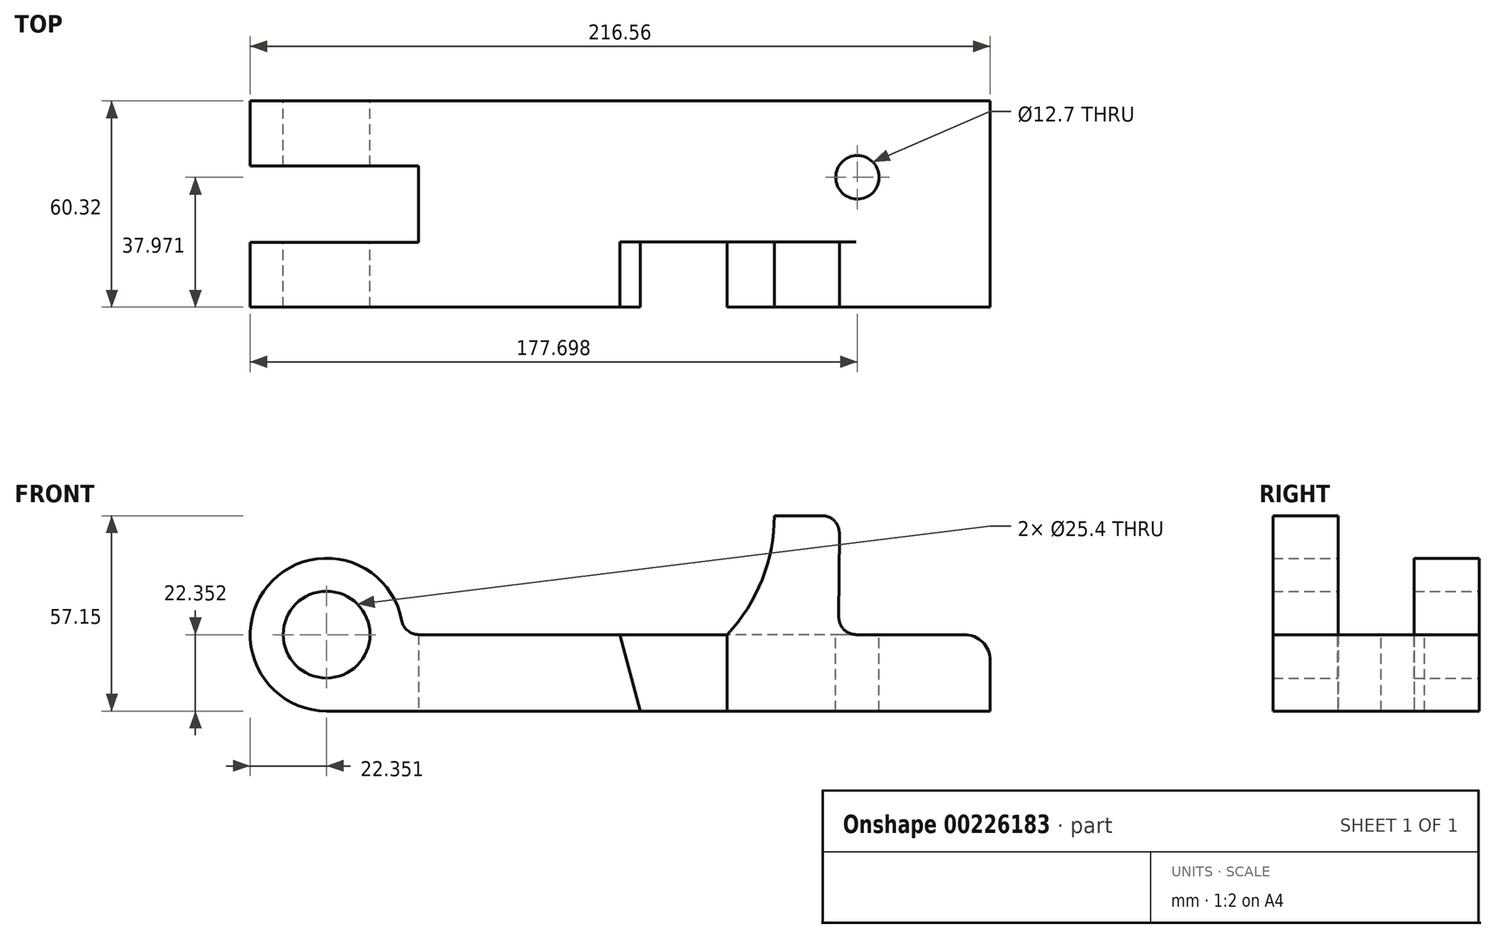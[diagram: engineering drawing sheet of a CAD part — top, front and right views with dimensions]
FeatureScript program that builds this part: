
annotation { "Feature Type Name" : "Feature", "Feature Type Description" : "" }
export const myFeature = defineFeature(function(context is Context, id is Id, definition is map)
    precondition{}
    {
        {
            var Q0;
            Q0=qCreatedBy(makeId("Front.planeOp"),FACE);
            var sketch = newSketch(context, id + "F0", { "sketchPlane" : qUnion([Q0])});
            skLineSegment(sketch, "E0.top", {"start": v(113.97, 22.35) * mm, "end": v(-57.89, 22.35) * mm});
            skLineSegment(sketch, "E0.left", {"start": v(113.97, 0) * mm, "end": v(113.97, 22.35) * mm});
            skCircle(sketch, "E1", {"center": v(-80.24, 22.35) * mm, "radius": 22.35 * mm});
            skCircle(sketch, "E2", {"center": v(-80.24, 22.35) * mm, "radius": 12.7 * mm});
            skLineSegment(sketch, "E3", {"start": v(-80.24, 0) * mm, "end": v(113.97, 0) * mm});
            skPoint(sketch, "E4", {"position": v(11.6, 0) * mm});
            skPoint(sketch, "E5", {"position": v(5.61, 22.35) * mm});
            skLineSegment(sketch, "E6", {"start": v(5.61, 22.35) * mm, "end": v(11.6, 0) * mm});
            skPoint(sketch, "E7", {"position": v(37, 0) * mm});
            skLineSegment(sketch, "E8", {"start": v(37, 0) * mm, "end": v(37, 22.35) * mm});
            skLineSegment(sketch, "E9.top", {"start": v(50.8, 57.15) * mm, "end": v(69.85, 57.15) * mm});
            skLineSegment(sketch, "E9.right", {"start": v(69.5, 0) * mm, "end": v(69.85, 57.15) * mm});
            skArc(sketch, "E10", {"start": v(37, 22.35) * mm, "mid": v(47.23, 38.43) * mm, "end": v(50.8, 57.15) * mm});
            skSolve(sketch);
        }
        {
            var Q0;
            {var subQ3=sQuery(id+"F0.wireOp",EDGE,"E6");Q0=makeQuery(id+"F0.imprint","IMPRINT",FACE,{"disambiguationData":[TD([[makeQuery(id+"F0.imprint","IMPRINT",EDGE,{"derivedFrom":subQ3}),-1.0]])]});}
            var Q1;
            {var subQ0=sQuery(id+"F0.wireOp",EDGE,"E8");Q1=makeQuery(id+"F0.imprint","IMPRINT",FACE,{"disambiguationData":[TD([[makeQuery(id+"F0.imprint","IMPRINT",EDGE,{"derivedFrom":subQ0}),-1.0]])]});}
            var Q2;
            {var subQ5=sQuery(id+"F0.wireOp",EDGE,"E9.bottom");Q2=makeQuery(id+"F0.imprint","IMPRINT",FACE,{"disambiguationData":[TD([[makeQuery(id+"F0.imprint","IMPRINT",EDGE,{"derivedFrom":subQ5}),1.0]])]});}
            var Q3;
            {var subQ0=sQuery(id+"F0.wireOp",EDGE,"E0.left");Q3=makeQuery(id+"F0.imprint","IMPRINT",FACE,{"disambiguationData":[TD([[makeQuery(id+"F0.imprint","IMPRINT",EDGE,{"derivedFrom":subQ0}),1.0]])]});}
            var Q4;
            Q4=makeQuery(id+"F0.imprint","IMPRINT",FACE,{"disambiguationData":[TD([[makeQuery(id+"F0.imprint","IMPRINT",EDGE,{"derivedFrom":sQuery(id+"F0.wireOp",EDGE,"E2")}),-1.0]])]});
            var Q5;
            {var subQ0=sQuery(id+"F0.wireOp",EDGE,"E6");Q5=makeQuery(id+"F0.imprint","IMPRINT",FACE,{"disambiguationData":[TD([[makeQuery(id+"F0.imprint","IMPRINT",EDGE,{"derivedFrom":subQ0}),1.0]])]});}
            var Q6;
            {var subQ4=sQuery(id+"F0.wireOp",EDGE,"E9.top");Q6=makeQuery(id+"F0.imprint","IMPRINT",FACE,{"disambiguationData":[TD([[makeQuery(id+"F0.imprint","IMPRINT",EDGE,{"derivedFrom":subQ4}),-1.0]])]});}
            extrude(context, id + "F1", {"entities" : qUnion([Q0, Q1, Q2, Q3, Q4, Q5, Q6]), "endBound" : BoundingType.SYMMETRIC, "depth" : 60.32 * mm});
        }
        {
            var Q0;
            Q0=makeQuery(id+"F1.opExtrude","CAP_FACE",FACE,{"disambiguationData":[OSD([sQuery(id+"F0.wireOp",EDGE,"E0.top"),sQuery(id+"F0.wireOp",EDGE,"E0.left"),sQuery(id+"F0.wireOp",EDGE,"E1"),sQuery(id+"F0.wireOp",EDGE,"E2"),sQuery(id+"F0.wireOp",EDGE,"E3"),sQuery(id+"F0.wireOp",EDGE,"E9.bottom"),sQuery(id+"F0.wireOp",EDGE,"E9.top"),sQuery(id+"F0.wireOp",EDGE,"E9.left"),sQuery(id+"F0.wireOp",EDGE,"E9.right")])],"isStart":false});
            var sketch = newSketch(context, id + "F2", { "sketchPlane" : qUnion([Q0])});
            skLineSegment(sketch, "E11", {"start": v(5.61, 22.35) * mm, "end": v(11.6, 0) * mm});
            skLineSegment(sketch, "E12", {"start": v(11.6, 0) * mm, "end": v(37, 0) * mm});
            skLineSegment(sketch, "E13", {"start": v(37, 0) * mm, "end": v(37, 22.35) * mm});
            skLineSegment(sketch, "E14", {"start": v(37, 22.35) * mm, "end": v(5.61, 22.35) * mm});
            skSolve(sketch);
        }
        {
            var Q0;
            Q0=makeQuery(id+"F1.opExtrude","CAP_FACE",FACE,{"disambiguationData":[OSD([sQuery(id+"F0.wireOp",EDGE,"E0.top"),sQuery(id+"F0.wireOp",EDGE,"E0.left"),sQuery(id+"F0.wireOp",EDGE,"E1"),sQuery(id+"F0.wireOp",EDGE,"E2"),sQuery(id+"F0.wireOp",EDGE,"E3"),sQuery(id+"F0.wireOp",EDGE,"E9.bottom"),sQuery(id+"F0.wireOp",EDGE,"E9.top"),sQuery(id+"F0.wireOp",EDGE,"E9.right"),sQuery(id+"F0.wireOp",EDGE,"crtvdxMS-Lb0s-6tKP-ZWnW-2UcVEUxHUHu2")])],"isStart":true});
            var sketch = newSketch(context, id + "F3", { "sketchPlane" : qUnion([Q0])});
            skLineSegment(sketch, "E15", {"start": v(-69.63, 22.35) * mm, "end": v(-37, 22.35) * mm});
            skLineSegment(sketch, "E16.0", {"start": v(-69.5, 0) * mm, "end": v(-69.85, 57.15) * mm});
            skLineSegment(sketch, "E17.0", {"start": v(-50.8, 57.15) * mm, "end": v(-69.85, 57.15) * mm});
            skSolve(sketch);
        }
        {
            var Q0;
            Q0=makeQuery(id+"F1.opExtrude","SWEPT_EDGE",EDGE,{"disambiguationData":[OSD([sQuery(id+"F0.wireOp",EDGE,"E9.top"),sQuery(id+"F0.wireOp",EDGE,"E9.right")])]});
            fillet(context, id + "F4", {"entities" : qUnion([Q0]), "radius" : 5.08 * mm, "tangentPropagation" : true, "allowEdgeOverflow" : false});
        }
        {
            var Q0;
            Q0=makeQuery(id+"F1.opExtrude","SWEPT_EDGE",EDGE,{"disambiguationData":[OSD([sQuery(id+"F0.wireOp",EDGE,"E0.top"),sQuery(id+"F0.wireOp",EDGE,"E0.left")])]});
            fillet(context, id + "F5", {"entities" : qUnion([Q0]), "radius" : 7.62 * mm, "tangentPropagation" : true, "allowEdgeOverflow" : false});
        }
        {
            var Q0;
            Q0=makeQuery(id+"F1.opExtrude","SWEPT_EDGE",EDGE,{"disambiguationData":[OSD([sQuery(id+"F0.wireOp",EDGE,"E0.top"),sQuery(id+"F0.wireOp",EDGE,"E1")])]});
            fillet(context, id + "F6", {"entities" : qUnion([Q0]), "radius" : 5.08 * mm, "tangentPropagation" : true, "allowEdgeOverflow" : false});
        }
        {
            var Q0;
            {var subQ0=sQuery(id+"F3.wireOp",EDGE,"E15");Q0=makeQuery(id+"F3.imprint","IMPRINT",FACE,{"disambiguationData":[TD([[makeQuery(id+"F3.imprint","IMPRINT",EDGE,{"derivedFrom":subQ0}),1.0]])]});}
            extrude(context, id + "F7", {"entities" : qUnion([Q0]), "operationType" : NewBodyOperationType.REMOVE, "oppositeDirection" : true, "depth" : 41.27 * mm});
        }
        {
            var Q0;
            {var subQ0=sQuery(id+"F0.wireOp",EDGE,"E0.top");var subQ1=makeQuery(id+"F0.imprint","INTERSECT",VERTEX,{"derivedFrom":[subQ0,sQuery(id+"F0.wireOp",EDGE,"E6")]});Q0=makeQuery(id+"F1.opExtrude","SWEPT_FACE",FACE,{"disambiguationData":[OSD([subQ0]),TDD([makeQuery(id+"F0.imprint","IMPRINT",EDGE,{"disambiguationData":[TD([[subQ1,1.0]])],"derivedFrom":subQ0}),makeQuery(id+"F0.imprint","IMPRINT",EDGE,{"disambiguationData":[TD([[makeQuery(id+"F0.imprint","INTERSECT",VERTEX,{"derivedFrom":[subQ0,sQuery(id+"F0.wireOp",EDGE,"E1")]}),1.0]])],"derivedFrom":subQ0})])]});}
            var sketch = newSketch(context, id + "F8", { "sketchPlane" : qUnion([Q0])});
            skSolve(sketch);
        }
        {
            var Q0;
            Q0=makeQuery(id+"F2.imprint","IMPRINT",FACE,{"disambiguationData":[TD([[makeQuery(id+"F2.imprint","IMPRINT",EDGE,{"derivedFrom":sQuery(id+"F2.wireOp",EDGE,"E11")}),1.0]])]});
            extrude(context, id + "F9", {"entities" : qUnion([Q0]), "operationType" : NewBodyOperationType.REMOVE, "oppositeDirection" : true, "depth" : 19.05 * mm});
        }
        {
            var Q0;
            Q0=makeQuery(id+"F1.opExtrude","SWEPT_EDGE",EDGE,{"disambiguationData":[OSD([sQuery(id+"F0.wireOp",EDGE,"E0.top"),sQuery(id+"F0.wireOp",EDGE,"E9.right")])]});
            fillet(context, id + "F10", {"entities" : qUnion([Q0]), "radius" : 5.08 * mm, "tangentPropagation" : true, "allowEdgeOverflow" : false});
        }
        {
            var Q0;
            Q0=qCreatedBy(makeId("Top.planeOp"),FACE);
            var sketch = newSketch(context, id + "F11", { "sketchPlane" : qUnion([Q0])});
            skLineSegment(sketch, "E18.0.0", {"start": v(-102.6, -30.16) * mm, "end": v(-58.27, -30.16) * mm});
            skLineSegment(sketch, "E18.0.1", {"start": v(-58.27, -30.16) * mm, "end": v(-58.27, 30.16) * mm});
            skLineSegment(sketch, "E18.0.2", {"start": v(-58.27, 30.16) * mm, "end": v(-102.6, 30.16) * mm});
            skLineSegment(sketch, "E18.0.3", {"start": v(-80.24, 30.16) * mm, "end": v(-80.24, -30.16) * mm});
            skLineSegment(sketch, "E19.0", {"start": v(-53.28, 30.16) * mm, "end": v(-53.28, -30.16) * mm});
            skLineSegment(sketch, "E20", {"start": v(-102.6, -30.16) * mm, "end": v(-102.6, 30.16) * mm});
            skLineSegment(sketch, "E21", {"start": v(-53.28, 11.16) * mm, "end": v(-102.6, 11.16) * mm});
            skLineSegment(sketch, "E22", {"start": v(-53.28, -11.16) * mm, "end": v(-102.6, -11.16) * mm});
            skSolve(sketch);
        }
        {
            var Q0;
            {var subQ0=sQuery(id+"F11.wireOp",EDGE,"E21");var subQ1=sQuery(id+"F11.wireOp",EDGE,"E18.0.3");var subQ2=makeQuery(id+"F11.imprint","INTERSECT",VERTEX,{"derivedFrom":[subQ1,subQ0]});Q0=makeQuery(id+"F11.imprint","IMPRINT",FACE,{"disambiguationData":[TD([[makeQuery(id+"F11.imprint","IMPRINT",EDGE,{"disambiguationData":[TD([[subQ2,-1.0]])],"derivedFrom":subQ1}),-1.0]])]});}
            var Q1;
            {var subQ0=sQuery(id+"F11.wireOp",EDGE,"E22");var subQ1=sQuery(id+"F11.wireOp",EDGE,"E18.0.1");var subQ2=makeQuery(id+"F11.imprint","INTERSECT",VERTEX,{"derivedFrom":[subQ1,subQ0]});Q1=makeQuery(id+"F11.imprint","IMPRINT",FACE,{"disambiguationData":[TD([[makeQuery(id+"F11.imprint","IMPRINT",EDGE,{"disambiguationData":[TD([[subQ2,-1.0]])],"derivedFrom":subQ1}),1.0]])]});}
            var Q2;
            {var subQ0=sQuery(id+"F11.wireOp",EDGE,"E22");var subQ1=sQuery(id+"F11.wireOp",EDGE,"E18.0.1");var subQ2=makeQuery(id+"F11.imprint","INTERSECT",VERTEX,{"derivedFrom":[subQ1,subQ0]});Q2=makeQuery(id+"F11.imprint","IMPRINT",FACE,{"disambiguationData":[TD([[makeQuery(id+"F11.imprint","IMPRINT",EDGE,{"disambiguationData":[TD([[subQ2,-1.0]])],"derivedFrom":subQ1}),-1.0]])]});}
            extrude(context, id + "F12", {"entities" : qUnion([Q0, Q1, Q2]), "operationType" : NewBodyOperationType.REMOVE, "endBound" : BoundingType.THROUGH_ALL, "depth" : 25.4 * mm});
        }
        {
            var Q0;
            {var subQ10=sQuery(id+"F3.wireOp",EDGE,"E15");Q0=makeQuery(id+"F8.imprint","IMPRINT",FACE,{"disambiguationData":[TD([[makeQuery(id+"F8.imprint","IMPRINT",EDGE,{"derivedFrom":makeQuery(id+"F7.boolean.opBoolean","COPY",EDGE,{"derivedFrom":makeQuery(id+"F7.opExtrude","CAP_EDGE",EDGE,{"disambiguationData":[OSD([subQ10])],"isStart":false})})}),-1.0]])]});}
            var sketch = newSketch(context, id + "F13", { "sketchPlane" : qUnion([Q0])});
            skCircle(sketch, "E23", {"center": v(75.1, 7.81) * mm, "radius": 6.35 * mm});
            skSolve(sketch);
        }
        {
            var Q0;
            Q0 = qSketchRegion(id + "F13", true);
            extrude(context, id + "F14", {"entities" : qUnion([Q0]), "operationType" : NewBodyOperationType.REMOVE, "endBound" : BoundingType.THROUGH_ALL, "oppositeDirection" : true, "depth" : 25.4 * mm});
        }
    });
